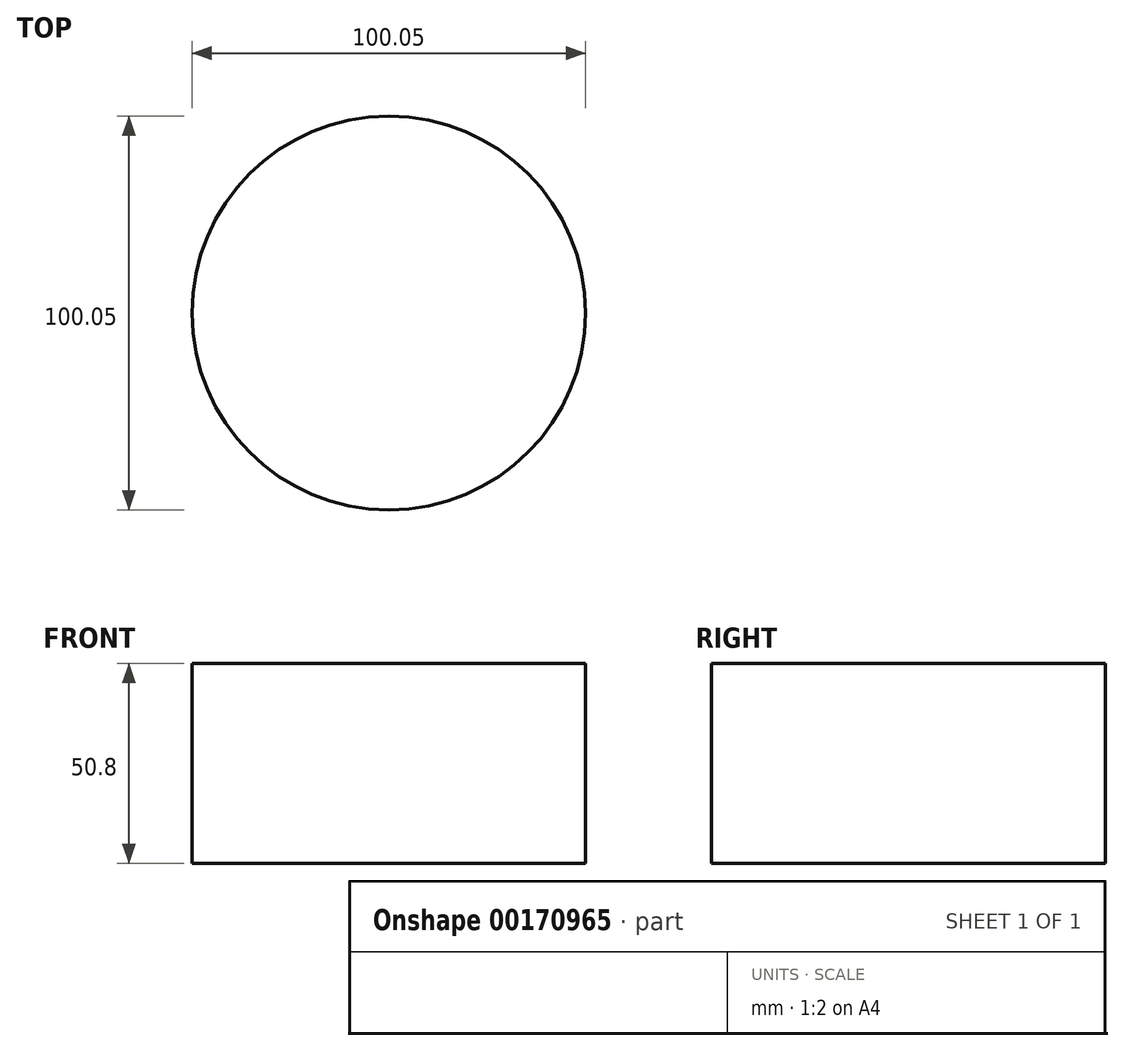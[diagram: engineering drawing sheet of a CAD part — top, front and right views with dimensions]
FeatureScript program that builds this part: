
annotation { "Feature Type Name" : "Feature", "Feature Type Description" : "" }
export const myFeature = defineFeature(function(context is Context, id is Id, definition is map)
    precondition{}
    {
        {
            var Q0;
            Q0=qCreatedBy(makeId("Top.planeOp"),FACE);
            var sketch = newSketch(context, id + "F0", { "sketchPlane" : qUnion([Q0])});
            skCircle(sketch, "E0", {"center": v(-44.07, 17.64) * mm, "radius": 50.03 * mm});
            skSolve(sketch);
        }
        {
            var Q0;
            Q0=makeQuery(id+"F0.imprint","IMPRINT",FACE,{"disambiguationData":[TD([[makeQuery(id+"F0.imprint","IMPRINT",EDGE,{"derivedFrom":sQuery(id+"F0.wireOp",EDGE,"E0")}),1.0]])]});
            var Q1;
            Q1 = qSketchRegion(id + "F0", true);
            extrude(context, id + "F1", {"entities" : qUnion([Q0, Q1]), "depth" : 50.8 * mm});
        }
    });
